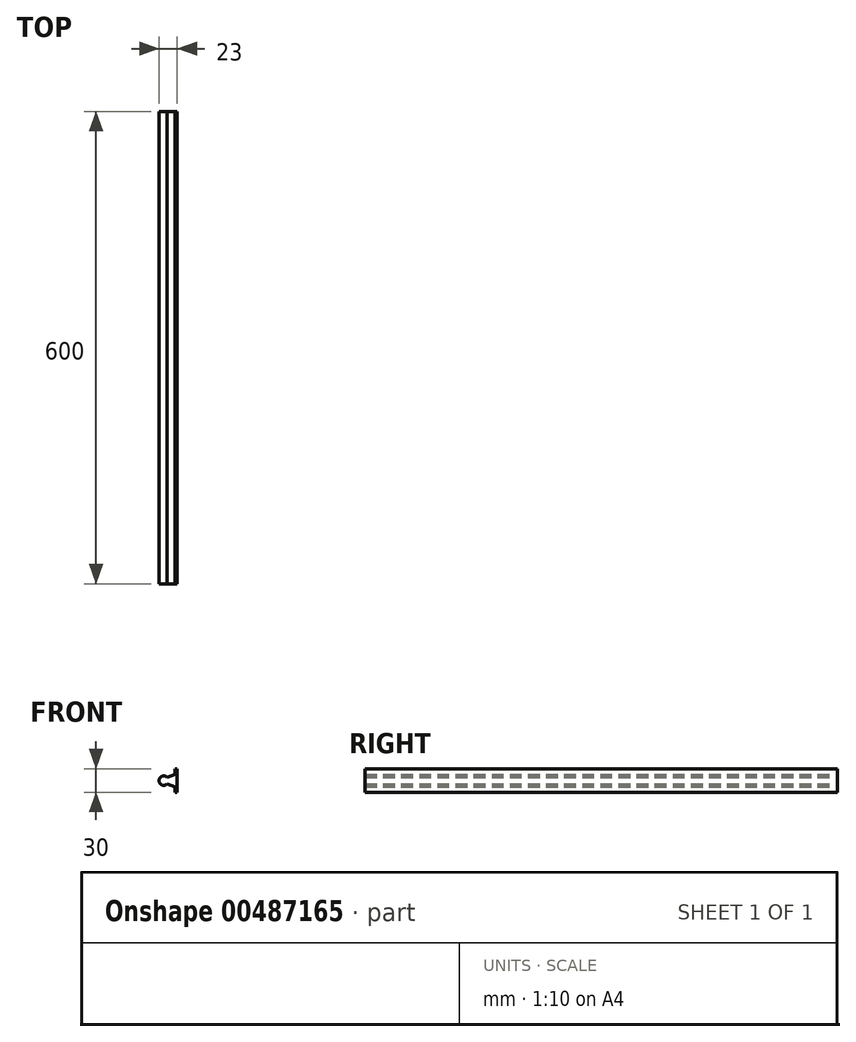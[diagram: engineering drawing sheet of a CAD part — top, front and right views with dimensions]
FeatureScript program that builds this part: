
annotation { "Feature Type Name" : "Feature", "Feature Type Description" : "" }
export const myFeature = defineFeature(function(context is Context, id is Id, definition is map)
    precondition{}
    {
        {
            var Q0;
            Q0=qCreatedBy(makeId("Front.planeOp"),FACE);
            var sketch = newSketch(context, id + "F0", { "sketchPlane" : qUnion([Q0])});
            skArc(sketch, "E0", {"start": v(4.47, 4) * mm, "mid": v(-6, 0) * mm, "end": v(4.47, -4) * mm});
            skLineSegment(sketch, "E1.bottom", {"start": v(14.5, 15) * mm, "end": v(17, 15) * mm});
            skLineSegment(sketch, "E1.top", {"start": v(14.5, -15) * mm, "end": v(17, -15) * mm});
            skLineSegment(sketch, "E1.left", {"start": v(14.5, 15) * mm, "end": v(14.5, 7.65) * mm});
            skLineSegment(sketch, "E1.right", {"start": v(17, 15) * mm, "end": v(17, -15) * mm});
            skLineSegment(sketch, "E2", {"start": v(4.47, 4) * mm, "end": v(14.5, 7.65) * mm});
            skLineSegment(sketch, "E3", {"start": v(4.47, -4) * mm, "end": v(14.5, -7.65) * mm});
            skLineSegment(sketch, "E4.trimOffspring", {"start": v(14.5, -7.65) * mm, "end": v(14.5, -15) * mm});
            skSolve(sketch);
        }
        {
            var Q0;
            Q0 = qSketchRegion(id + "F0", true);
            extrude(context, id + "F1", {"entities" : qUnion([Q0]), "depth" : 300 * mm, "hasSecondDirection" : true, "secondDirectionOppositeDirection" : true, "secondDirectionDepth" : 300 * mm});
        }
    });
